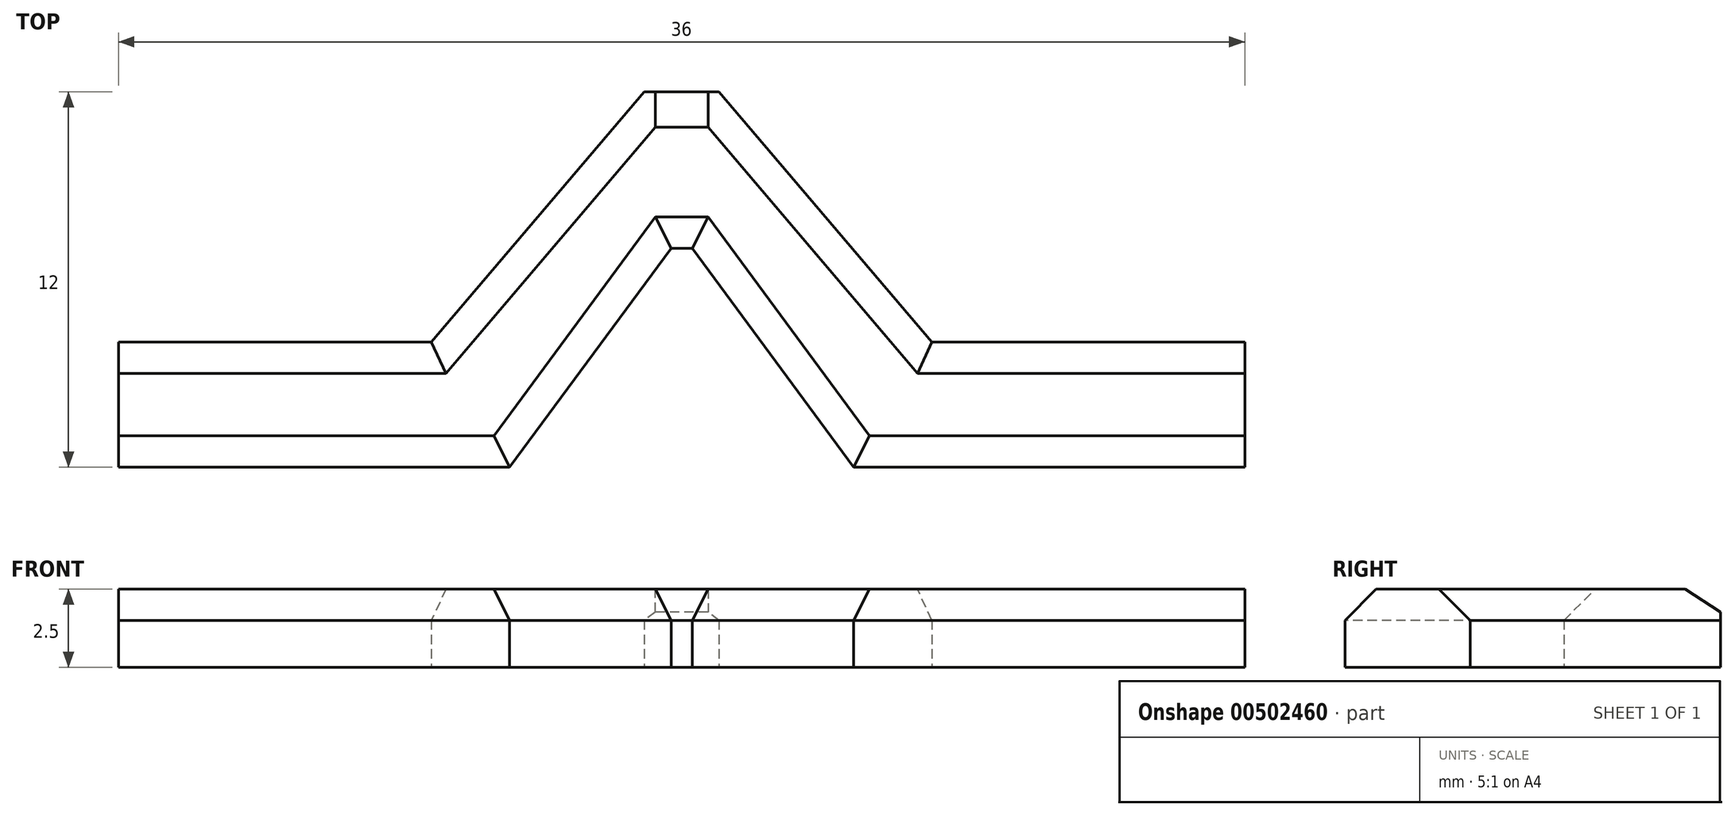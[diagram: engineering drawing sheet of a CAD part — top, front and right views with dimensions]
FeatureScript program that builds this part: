
annotation { "Feature Type Name" : "Feature", "Feature Type Description" : "" }
export const myFeature = defineFeature(function(context is Context, id is Id, definition is map)
    precondition{}
    {
        {
            var Q0;
            Q0=qCreatedBy(makeId("Top.planeOp"),FACE);
            var sketch = newSketch(context, id + "F0", { "sketchPlane" : qUnion([Q0])});
            skLineSegment(sketch, "E0.bottom", {"start": v(-18, 2) * mm, "end": v(-13, 2) * mm});
            skLineSegment(sketch, "E0.top", {"start": v(-18, -7) * mm, "end": v(18, -7) * mm});
            skLineSegment(sketch, "E0.left", {"start": v(-18, 2) * mm, "end": v(-18, -7) * mm});
            skLineSegment(sketch, "E0.right", {"start": v(18, 2) * mm, "end": v(18, -7) * mm});
            skLineSegment(sketch, "E1.top", {"start": v(-13, 7) * mm, "end": v(13, 7) * mm});
            skLineSegment(sketch, "E1.left", {"start": v(-13, 2) * mm, "end": v(-13, 7) * mm});
            skLineSegment(sketch, "E1.right", {"start": v(13, 2) * mm, "end": v(13, 7) * mm});
            skLineSegment(sketch, "E2.trimOffspring", {"start": v(13, 2) * mm, "end": v(18, 2) * mm});
            skLineSegment(sketch, "E3", {"start": v(0, 32.2) * mm, "end": v(0, 0) * mm, "construction": true});
            skLineSegment(sketch, "E4", {"start": v(0, 0) * mm, "end": v(50.2, 0) * mm, "construction": true});
            skSolve(sketch);
        }
        {
            var Q0;
            Q0=makeQuery(id+"F0.imprint","IMPRINT",FACE,{"disambiguationData":[TD([[makeQuery(id+"F0.imprint","IMPRINT",EDGE,{"derivedFrom":sQuery(id+"F0.wireOp",EDGE,"E0.bottom")}),-1.0]])]});
            var sketch = newSketch(context, id + "F1", { "sketchPlane" : qUnion([Q0])});
            skLineSegment(sketch, "E5.0.0", {"start": v(-13, 2) * mm, "end": v(-18, 2) * mm});
            skLineSegment(sketch, "E5.0.1", {"start": v(-18, 2) * mm, "end": v(-18, -7) * mm});
            skLineSegment(sketch, "E5.0.2", {"start": v(-18, -7) * mm, "end": v(18, -7) * mm});
            skLineSegment(sketch, "E5.0.3", {"start": v(18, -7) * mm, "end": v(18, 2) * mm});
            skLineSegment(sketch, "E5.0.4", {"start": v(18, 2) * mm, "end": v(13, 2) * mm});
            skLineSegment(sketch, "E5.0.5", {"start": v(13, 2) * mm, "end": v(13, 7) * mm});
            skLineSegment(sketch, "E5.0.6", {"start": v(13, 7) * mm, "end": v(-13, 7) * mm});
            skLineSegment(sketch, "E5.0.7", {"start": v(-13, 7) * mm, "end": v(-13, 2) * mm});
            skLineSegment(sketch, "E6", {"start": v(-18, -5) * mm, "end": v(-5.5, -5) * mm});
            skLineSegment(sketch, "E7", {"start": v(-5.5, -5) * mm, "end": v(-0.34, 2) * mm});
            skLineSegment(sketch, "E8", {"start": v(-0.34, 2) * mm, "end": v(0, 2) * mm});
            skLineSegment(sketch, "E9", {"start": v(-18, -1) * mm, "end": v(-8, -1) * mm});
            skLineSegment(sketch, "E10", {"start": v(-8, -1) * mm, "end": v(-1.2, 7) * mm});
            skLineSegment(sketch, "E11", {"start": v(0, 7) * mm, "end": v(0, 2) * mm});
            skLineSegment(sketch, "E12", {"start": v(-18, -5) * mm, "end": v(-18, -1) * mm});
            skLineSegment(sketch, "E13", {"start": v(-1.2, 7) * mm, "end": v(0, 7) * mm});
            skSolve(sketch);
        }
        {
            var Q0;
            {var subQ0=sQuery(id+"F1.wireOp",EDGE,"E6");Q0=makeQuery(id+"F1.imprint","IMPRINT",FACE,{"disambiguationData":[TD([[makeQuery(id+"F1.imprint","IMPRINT",EDGE,{"derivedFrom":subQ0}),1.0]])]});}
            extrude(context, id + "F2", {"entities" : qUnion([Q0]), "depth" : 2.5 * mm, "offsetDistance" : 25 * mm});
        }
        {
            var Q0;
            Q0=makeQuery(id+"F2.opExtrude","SWEPT_BODY",BODY,{"disambiguationData":[OSD([sQuery(id+"F1.wireOp",EDGE,"E5.0.1"),sQuery(id+"F1.wireOp",EDGE,"E6"),sQuery(id+"F1.wireOp",EDGE,"E7"),sQuery(id+"F1.wireOp",EDGE,"E8"),sQuery(id+"F1.wireOp",EDGE,"E9"),sQuery(id+"F1.wireOp",EDGE,"E10"),sQuery(id+"F1.wireOp",EDGE,"E11")])]});
            var Q1;
            Q1=qCreatedBy(makeId("Right.planeOp"),FACE);
            mirror(context, id + "F3", {"operationType" : NewBodyOperationType.ADD, "entities" : qUnion([Q0]), "mirrorPlane" : qUnion([Q1])});
        }
        {
            var Q0;
            Q0=makeQuery(id+"F2.opExtrude","CAP_EDGE",EDGE,{"disambiguationData":[OSD([sQuery(id+"F1.wireOp",EDGE,"E6")])],"isStart":false});
            var Q1;
            Q1=makeQuery(id+"F2.opExtrude","CAP_EDGE",EDGE,{"disambiguationData":[OSD([sQuery(id+"F1.wireOp",EDGE,"E9")])],"isStart":false});
            var Q2;
            Q2=makeQuery(id+"F2.opExtrude","CAP_EDGE",EDGE,{"disambiguationData":[OSD([sQuery(id+"F1.wireOp",EDGE,"E10")])],"isStart":false});
            var Q3;
            Q3=makeQuery(id+"F2.opExtrude","CAP_EDGE",EDGE,{"disambiguationData":[OSD([sQuery(id+"F1.wireOp",EDGE,"E7")])],"isStart":false});
            var Q4;
            Q4=makeQuery(id+"F3.opPattern","COPY",EDGE,{"derivedFrom":makeQuery(id+"F2.opExtrude","CAP_EDGE",EDGE,{"disambiguationData":[OSD([sQuery(id+"F1.wireOp",EDGE,"E7")])],"isStart":false}),"instanceName":"1"});
            var Q5;
            Q5=makeQuery(id+"F3.opPattern","COPY",EDGE,{"derivedFrom":makeQuery(id+"F2.opExtrude","CAP_EDGE",EDGE,{"disambiguationData":[OSD([sQuery(id+"F1.wireOp",EDGE,"E10")])],"isStart":false}),"instanceName":"1"});
            var Q6;
            Q6=makeQuery(id+"F3.opPattern","COPY",EDGE,{"derivedFrom":makeQuery(id+"F2.opExtrude","CAP_EDGE",EDGE,{"disambiguationData":[OSD([sQuery(id+"F1.wireOp",EDGE,"E9")])],"isStart":false}),"instanceName":"1"});
            var Q7;
            Q7=makeQuery(id+"F3.opPattern","COPY",EDGE,{"derivedFrom":makeQuery(id+"F2.opExtrude","CAP_EDGE",EDGE,{"disambiguationData":[OSD([sQuery(id+"F1.wireOp",EDGE,"E6")])],"isStart":false}),"instanceName":"1"});
            var Q8;
            {var subQ0=makeQuery(id+"F2.opExtrude","CAP_EDGE",EDGE,{"disambiguationData":[OSD([sQuery(id+"F1.wireOp",EDGE,"E8")])],"isStart":false});Q8=makeQuery(id+"F3.boolean.opBoolean","MERGE",EDGE,{"derivedFrom":[subQ0,makeQuery(id+"F3.opPattern","COPY",EDGE,{"derivedFrom":subQ0,"instanceName":"1"})]});}
            chamfer(context, id + "F4", {"entities" : qUnion([Q0, Q1, Q2, Q3, Q4, Q5, Q6, Q7, Q8]), "width" : 1 * mm, "tangentPropagation" : true});
        }
        {
            var Q0;
            {var subQ0=makeQuery(id+"F2.opExtrude","CAP_EDGE",EDGE,{"disambiguationData":[OSD([sQuery(id+"F1.wireOp",EDGE,"E10")])],"isStart":false});Q0=makeQuery(id+"F4.opChamfer","BLEND_EDGE",EDGE,{"blendedFrom":[subQ0,makeQuery(id+"F3.opPattern","COPY",EDGE,{"derivedFrom":subQ0,"instanceName":"1"})],"blendedInto":[]});}
            chamfer(context, id + "F5", {"entities" : qUnion([Q0]), "width" : 1 * mm, "tangentPropagation" : true});
        }
    });
